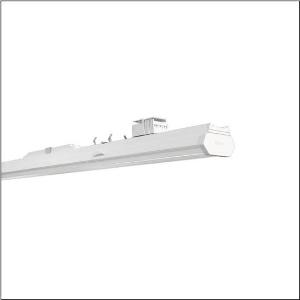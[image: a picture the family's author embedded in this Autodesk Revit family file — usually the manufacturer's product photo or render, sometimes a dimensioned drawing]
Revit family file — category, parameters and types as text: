
# Revit family: licross_r__21_protected_mo_52td11dn48xg_0db0
name_source: partatom
category: Lighting Fixtures
units: mm (PartAtom-declared; Revit-internal decimal feet)

## family parameters
Cut with Voids When Loaded = No
Host = Face
Light Source = No
Part Type = Normal
Room Calculation Point = No
Round Connector Dimension = Use Diameter
Shared = No

## types (1)
- --- (1 x LED, 8000 lm, 45.5 W, 4000K)
    Apparent Load = 46 VA
    CIE Flux Codes = 83 94 98 100 100
    Color Rendering = 80
    Color Temperature = 4000K
    Default Elevation = 1800 mm
    Description = Licross® 21 Protected MO, luminaire insert, of sheet steel, galvanised, coil coated, white, length: 1.500mm, width: 90mm, height: 103mm, LED rated luminous flux: 8.000lm, light colour: 840, control gear: DALI 2, with plug, 5-pole, with phase selection, mains connection: 220..240V, AC, 50/60Hz, rated input power: 46W, halogen-free wiring, primary light control with lens, of plastic, primary optical cover: cover, of PMMA, light emission: direct distribution, primary light characteristic: symmetric, protection rating (complete): IP54, insulation class (complete): insulation class I (protective earthing), certification: CE, ENEC, VDE, UKCA, protection symbol: D if used in an environment with non-conductive dust loads with corresponding accessories, impact resistance: IK06, permissible ambient temperature for indoor applications: -25..+45°C, corresponds to IFS (International Featured Standards) requirements for safety and quality in the food industry, reducing of maximum allowable ambient temperature of 5°C with ceiling mounting, LABS conformity tested according to VDMA 24364:2018-05, packaging unit: 1 piece
    Height = 92 mm
    Lamp = 1 x LED
    Lamp Light Flux = 8000 lm
    Lamp Power = 45.5 W
    Lamp count = 1
    Length = 1500 mm
    Luminous efficacy = 176 lm/W
    Manufacturer = Siteco
    ModVariant = No
    Model = 52TD11DN48XG
    Mounting Place = Ceiling
    Mounting Type = Pendant
    Number of Poles = 1
    OnlyDefault = Yes
    Power Factor = 1
    Product Name = Licross® 21 Protected MO
    Product group = luminaire insert
    ProductGroupID = 901
    Protection Class = Protection class I
    Protection Degree = IP 54
    RLX_Detail_Level = 1
    RLX_Emergency_Light_Flux = 0 lm
    RLX_Emergency_Type = 0
    RLX_Emergency_Type_DB = No
    RlxData = <blob elided: 24073 chars, md5=049daef7>
    Socket = socket
    Standby Power = 0 W
    System Light Flux = 8000 lm
    System Power = 46 W
    Type Comments = factory setting: luminous flux: 100 % | dim-lin: 254 | 307 mA
    Type Image = l_1256148.jpg
    URL = http://relux.com
    VarID = @adj_077951
    Voltage = 0 V
    Weight = 0.00 kg
    Width = 88 mm

## geometry (parser evidence)
native form markers: Blend x4, Sweep x10
no freeform markers — native parametric forms only
